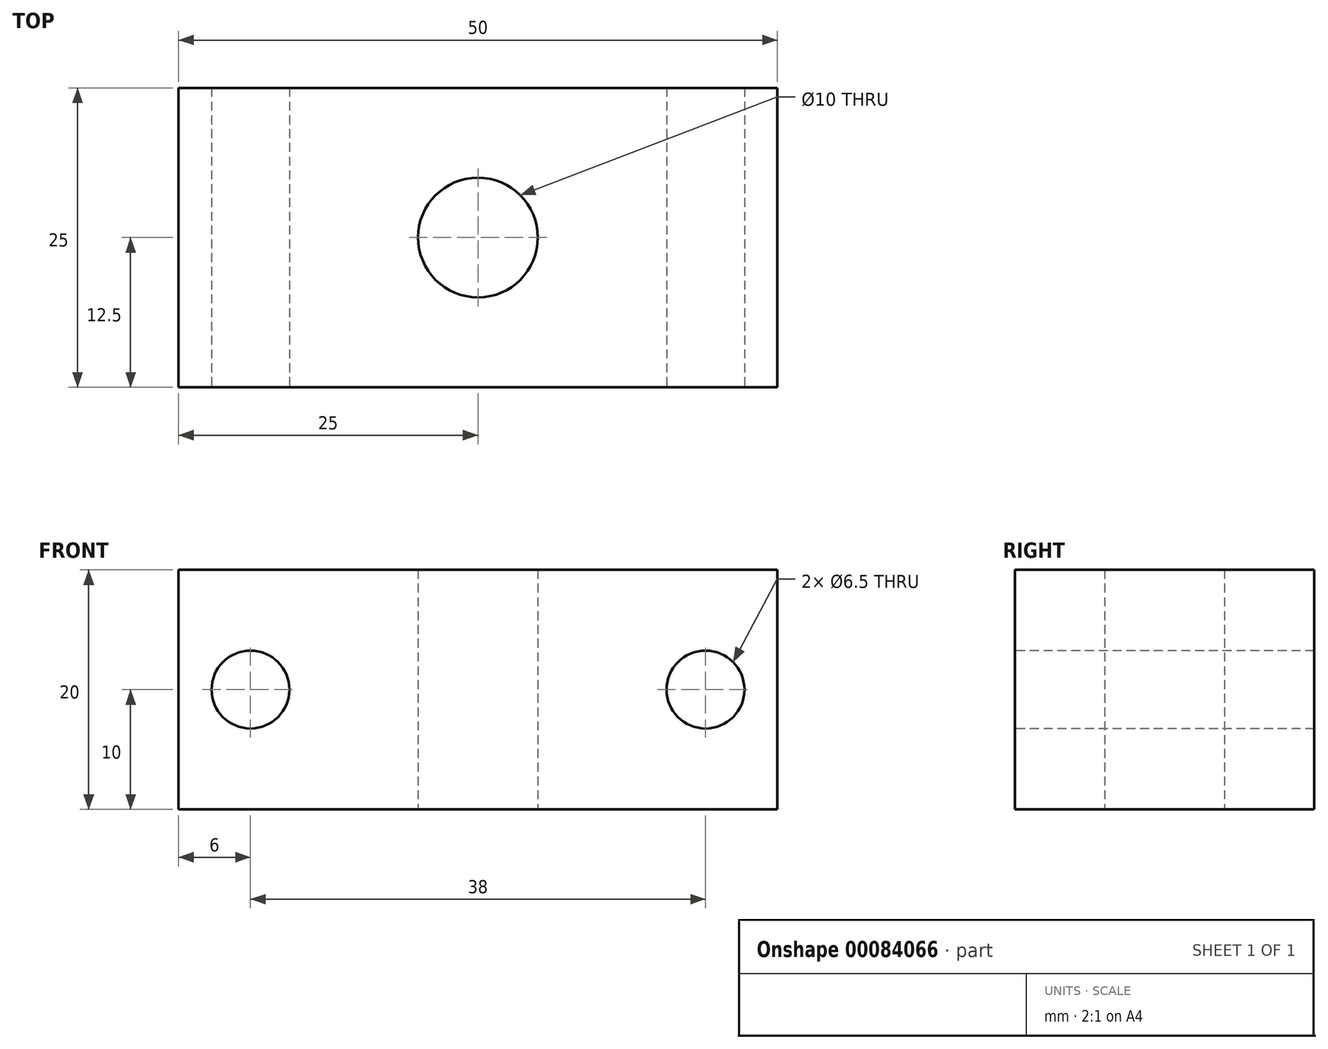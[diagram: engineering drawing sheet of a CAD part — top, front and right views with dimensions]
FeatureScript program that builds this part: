
annotation { "Feature Type Name" : "Feature", "Feature Type Description" : "" }
export const myFeature = defineFeature(function(context is Context, id is Id, definition is map)
    precondition{}
    {
        {
            var Q0;
            Q0=qCreatedBy(makeId("Front.planeOp"),FACE);
            var sketch = newSketch(context, id + "F0", { "sketchPlane" : qUnion([Q0])});
            skLineSegment(sketch, "E0.bottom", {"start": v(0, 0) * mm, "end": v(50, 0) * mm});
            skLineSegment(sketch, "E0.top", {"start": v(0, 20) * mm, "end": v(50, 20) * mm});
            skLineSegment(sketch, "E0.left", {"start": v(0, 0) * mm, "end": v(0, 20) * mm});
            skLineSegment(sketch, "E0.right", {"start": v(50, 0) * mm, "end": v(50, 20) * mm});
            skCircle(sketch, "E1", {"center": v(6, 10) * mm, "radius": 3.25 * mm});
            skCircle(sketch, "E2", {"center": v(44, 10) * mm, "radius": 3.25 * mm});
            skSolve(sketch);
        }
        {
            var Q0;
            Q0 = qSketchRegion(id + "F0", true);
            extrude(context, id + "F1", {"entities" : qUnion([Q0]), "oppositeDirection" : true, "depth" : 25 * mm});
        }
        {
            var Q0;
            Q0=qCreatedBy(makeId("Top.planeOp"),FACE);
            var sketch = newSketch(context, id + "F2", { "sketchPlane" : qUnion([Q0])});
            skCircle(sketch, "E3", {"center": v(25, 12.5) * mm, "radius": 5 * mm});
            skLineSegment(sketch, "E4", {"start": v(0, 0) * mm, "end": v(0, 25) * mm});
            skSolve(sketch);
        }
        {
            var Q0;
            Q0 = qSketchRegion(id + "F2", true);
            var Q1;
            Q1=makeQuery(id+"F2.imprint","IMPRINT",FACE,{"disambiguationData":[TD([[makeQuery(id+"F2.imprint","IMPRINT",EDGE,{"derivedFrom":sQuery(id+"F2.wireOp",EDGE,"E3")}),1.0]])]});
            extrude(context, id + "F3", {"entities" : qUnion([Q0, Q1]), "depth" : 20 * mm});
        }
        {
            var Q0;
            Q0=makeQuery(id+"F3.opExtrude","SWEPT_BODY",BODY,{"disambiguationData":[OSD([sQuery(id+"F2.wireOp",EDGE,"E3")])]});
            var Q1;
            Q1=makeQuery(id+"F1.opExtrude","SWEPT_BODY",BODY,{"disambiguationData":[OSD([sQuery(id+"F0.wireOp",EDGE,"E0.bottom"),sQuery(id+"F0.wireOp",EDGE,"E0.top"),sQuery(id+"F0.wireOp",EDGE,"E0.left"),sQuery(id+"F0.wireOp",EDGE,"E0.right"),sQuery(id+"F0.wireOp",EDGE,"E1"),sQuery(id+"F0.wireOp",EDGE,"E2")])]});
            booleanBodies(context, id + "F4", {"operationType" : BooleanOperationType.SUBTRACTION, "tools" : qUnion([Q0]), "targets" : qUnion([Q1])});
        }
    });
